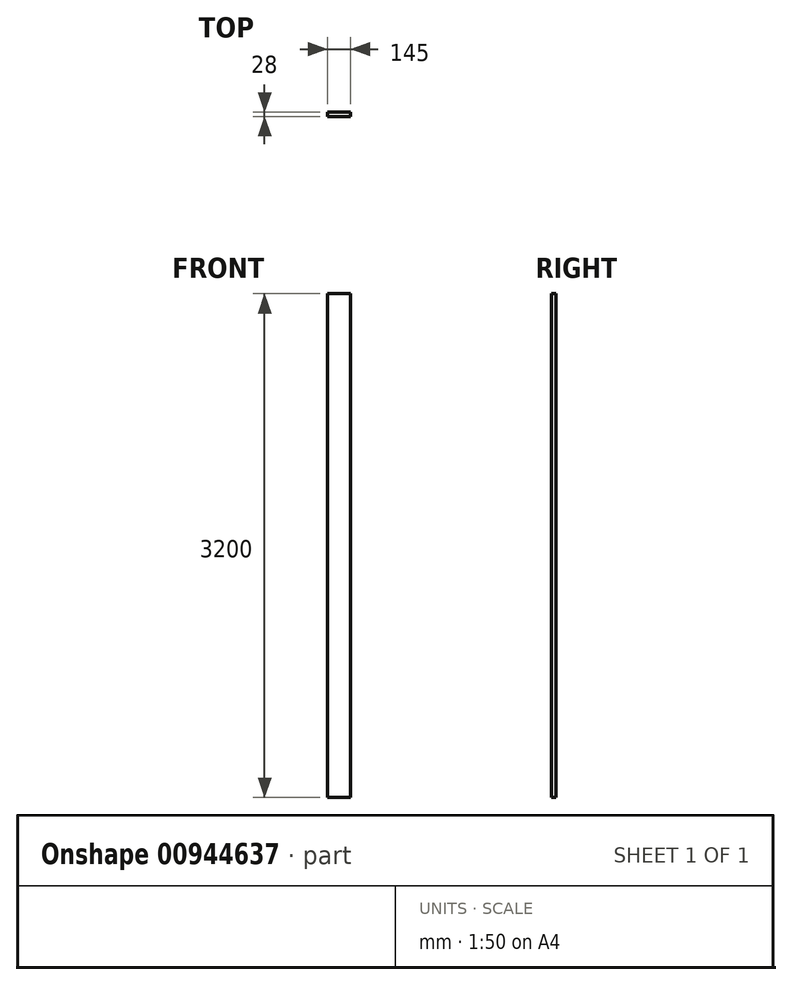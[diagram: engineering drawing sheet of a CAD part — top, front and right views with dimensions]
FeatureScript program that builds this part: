
annotation { "Feature Type Name" : "Feature", "Feature Type Description" : "" }
export const myFeature = defineFeature(function(context is Context, id is Id, definition is map)
    precondition{}
    {
        {
            var Q0;
            Q0=qCreatedBy(makeId("Top.planeOp"),FACE);
            var sketch = newSketch(context, id + "F0", { "sketchPlane" : qUnion([Q0])});
            skLineSegment(sketch, "E0.bottom", {"start": v(0, 0) * mm, "end": v(145, 0) * mm});
            skLineSegment(sketch, "E0.top", {"start": v(0, 28) * mm, "end": v(145, 28) * mm});
            skLineSegment(sketch, "E0.left", {"start": v(0, 0) * mm, "end": v(0, 28) * mm});
            skLineSegment(sketch, "E0.right", {"start": v(145, 0) * mm, "end": v(145, 28) * mm});
            skSolve(sketch);
        }
        {
            var Q0;
            Q0=makeQuery(id+"F0.imprint","IMPRINT",FACE,{"disambiguationData":[TD([[makeQuery(id+"F0.imprint","IMPRINT",EDGE,{"derivedFrom":sQuery(id+"F0.wireOp",EDGE,"E0.bottom")}),1.0]])]});
            extrude(context, id + "F1", {"entities" : qUnion([Q0]), "depth" : 3200 * mm, "offsetDistance" : 25 * mm});
        }
    });
